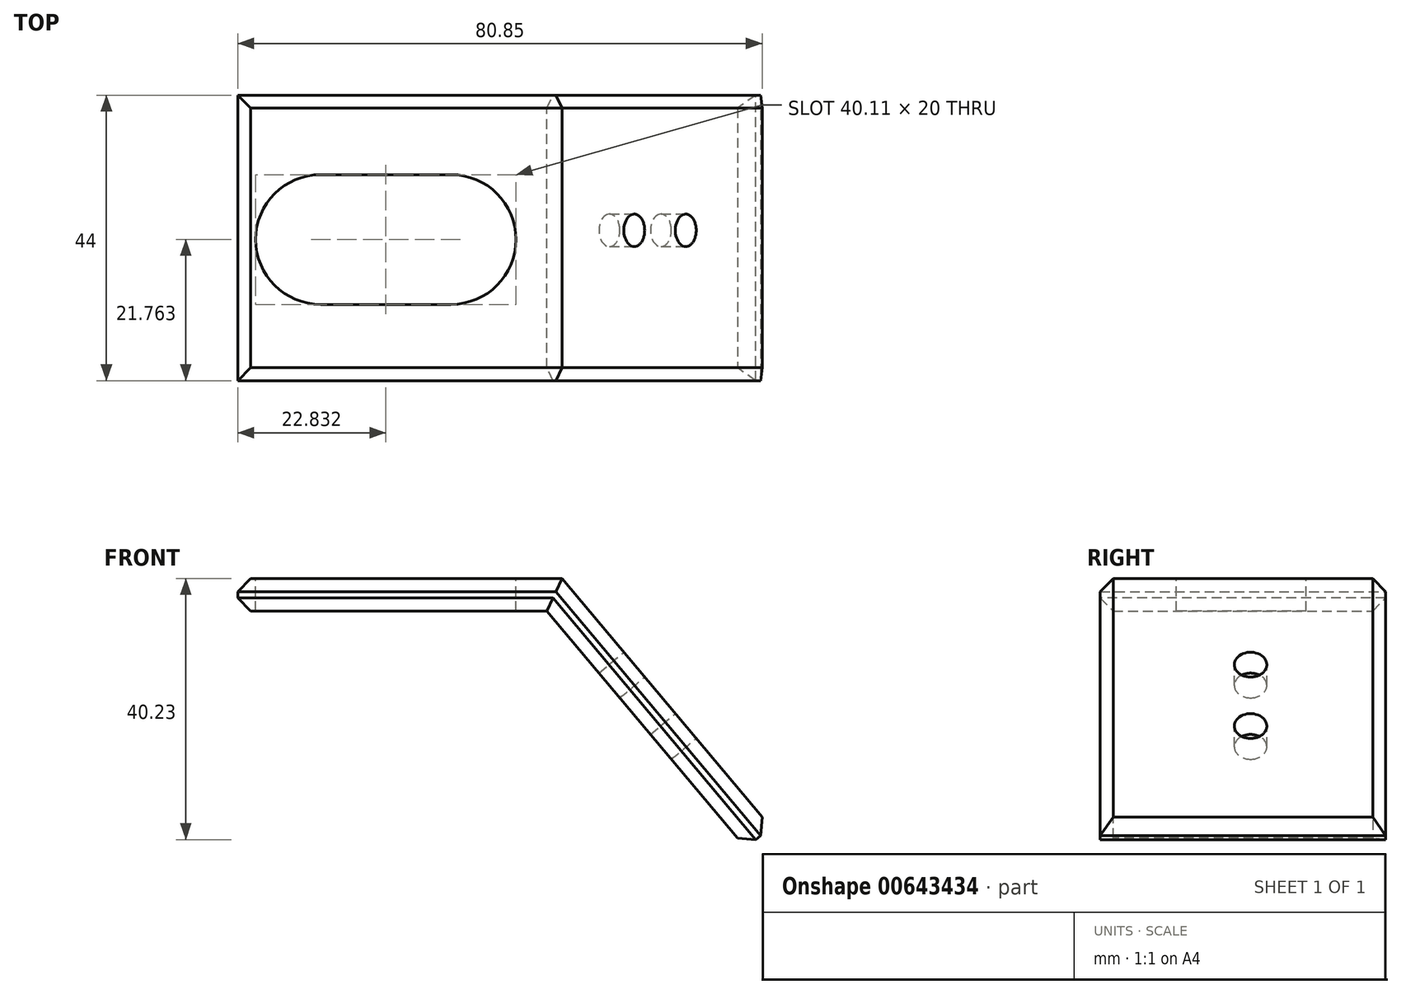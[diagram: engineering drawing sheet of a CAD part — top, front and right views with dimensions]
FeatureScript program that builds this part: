
annotation { "Feature Type Name" : "Feature", "Feature Type Description" : "" }
export const myFeature = defineFeature(function(context is Context, id is Id, definition is map)
    precondition{}
    {
        {
            var Q0;
            Q0=qCreatedBy(makeId("Front.planeOp"),FACE);
            var sketch = newSketch(context, id + "F0", { "sketchPlane" : qUnion([Q0])});
            skLineSegment(sketch, "E0", {"start": v(0, 0) * mm, "end": v(50, 0) * mm});
            skLineSegment(sketch, "E1", {"start": v(50, 0) * mm, "end": v(82.14, -38.3) * mm});
            skLineSegment(sketch, "E2.0", {"start": v(47.67, -5) * mm, "end": v(78.3, -41.52) * mm});
            skLineSegment(sketch, "E2.1", {"start": v(0, -5) * mm, "end": v(47.67, -5) * mm});
            skLineSegment(sketch, "E3", {"start": v(0, 0) * mm, "end": v(0, -5) * mm});
            skLineSegment(sketch, "E4", {"start": v(78.3, -41.52) * mm, "end": v(82.14, -38.3) * mm});
            skSolve(sketch);
        }
        {
            var Q0;
            Q0 = qSketchRegion(id + "F0", true);
            extrude(context, id + "F1", {"entities" : qUnion([Q0]), "depth" : 44 * mm, "offsetDistance" : 25 * mm});
        }
        {
            var Q0;
            Q0=makeQuery(id+"F1.opExtrude","SWEPT_FACE",FACE,{"disambiguationData":[OSD([sQuery(id+"F0.wireOp",EDGE,"E0")])]});
            var sketch = newSketch(context, id + "F2", { "sketchPlane" : qUnion([Q0])});
            skLineSegment(sketch, "E5", {"start": v(12.78, -22.24) * mm, "end": v(32.89, -22.24) * mm});
            skArc(sketch, "E6.0.startCap", {"start": v(12.78, -32.24) * mm, "mid": v(2.78, -22.24) * mm, "end": v(12.78, -12.24) * mm});
            skArc(sketch, "E6.0.endCap", {"start": v(32.89, -12.24) * mm, "mid": v(42.89, -22.24) * mm, "end": v(32.89, -32.24) * mm});
            skLineSegment(sketch, "E6.0.left", {"start": v(12.78, -12.24) * mm, "end": v(32.89, -12.24) * mm});
            skLineSegment(sketch, "E6.0.right", {"start": v(12.78, -32.24) * mm, "end": v(32.89, -32.24) * mm});
            skSolve(sketch);
        }
        {
            var Q0;
            Q0 = qSketchRegion(id + "F2", true);
            extrude(context, id + "F3", {"entities" : qUnion([Q0]), "operationType" : NewBodyOperationType.REMOVE, "oppositeDirection" : true, "depth" : 25 * mm, "offsetDistance" : 25 * mm});
        }
        {
            var Q0;
            Q0=makeQuery(id+"F1.opExtrude","SWEPT_FACE",FACE,{"disambiguationData":[OSD([sQuery(id+"F0.wireOp",EDGE,"E1")])]});
            var sketch = newSketch(context, id + "F4", { "sketchPlane" : qUnion([Q0])});
            skPoint(sketch, "E7", {"position": v(-20.82, -49.46) * mm});
            skPoint(sketch, "E8", {"position": v(-20.82, -61.8) * mm});
            skSolve(sketch);
        }
        {
            var Q0;
            Q0=sQuery(id+"F4.wireOp",VERTEX,"E7");
            var Q1;
            Q1=sQuery(id+"F4.wireOp",VERTEX,"E8");
            var Q2;
            Q2=makeQuery(id+"F1.opExtrude","SWEPT_BODY",BODY,{"disambiguationData":[OSD([sQuery(id+"F0.wireOp",EDGE,"E0"),sQuery(id+"F0.wireOp",EDGE,"E1"),sQuery(id+"F0.wireOp",EDGE,"E2.0"),sQuery(id+"F0.wireOp",EDGE,"E2.1"),sQuery(id+"F0.wireOp",EDGE,"E3"),sQuery(id+"F0.wireOp",EDGE,"E4")])]});
            hole(context, id + "F5", {"style" : HoleStyle.SIMPLE, "endStyle" : HoleEndStyle.THROUGH, "holeDiameter" : 5 * mm, "majorDiameter" : 5 * mm, "isTappedThrough" : true, "tappedDepth" : 12 * mm, "tapClearance" : 3, "locations" : qUnion([Q0, Q1]), "scope" : qUnion([Q2])});
        }
        {
            var Q0;
            Q0=makeQuery(id+"F1.opExtrude","CAP_EDGE",EDGE,{"disambiguationData":[OSD([sQuery(id+"F0.wireOp",EDGE,"E1")])],"isStart":false});
            var Q1;
            Q1=makeQuery(id+"F1.opExtrude","CAP_EDGE",EDGE,{"disambiguationData":[OSD([sQuery(id+"F0.wireOp",EDGE,"E2.0")])],"isStart":false});
            var Q2;
            Q2=makeQuery(id+"F1.opExtrude","SWEPT_EDGE",EDGE,{"disambiguationData":[OSD([sQuery(id+"F0.wireOp",EDGE,"E2.0"),sQuery(id+"F0.wireOp",EDGE,"E4")])]});
            var Q3;
            Q3=makeQuery(id+"F1.opExtrude","SWEPT_EDGE",EDGE,{"disambiguationData":[OSD([sQuery(id+"F0.wireOp",EDGE,"E1"),sQuery(id+"F0.wireOp",EDGE,"E4")])]});
            var Q4;
            Q4=makeQuery(id+"F1.opExtrude","CAP_EDGE",EDGE,{"disambiguationData":[OSD([sQuery(id+"F0.wireOp",EDGE,"E1")])],"isStart":true});
            var Q5;
            Q5=makeQuery(id+"F1.opExtrude","CAP_EDGE",EDGE,{"disambiguationData":[OSD([sQuery(id+"F0.wireOp",EDGE,"E2.0")])],"isStart":true});
            chamfer(context, id + "F6", {"entities" : qUnion([Q0, Q1, Q2, Q3, Q4, Q5]), "width" : 2 * mm, "tangentPropagation" : true});
        }
        {
            var Q0;
            Q0=makeQuery(id+"F1.opExtrude","CAP_EDGE",EDGE,{"disambiguationData":[OSD([sQuery(id+"F0.wireOp",EDGE,"E0")])],"isStart":true});
            var Q1;
            Q1=makeQuery(id+"F1.opExtrude","CAP_EDGE",EDGE,{"disambiguationData":[OSD([sQuery(id+"F0.wireOp",EDGE,"E2.1")])],"isStart":true});
            var Q2;
            Q2=makeQuery(id+"F1.opExtrude","SWEPT_EDGE",EDGE,{"disambiguationData":[OSD([sQuery(id+"F0.wireOp",EDGE,"E0"),sQuery(id+"F0.wireOp",EDGE,"E3")])]});
            var Q3;
            Q3=makeQuery(id+"F1.opExtrude","SWEPT_EDGE",EDGE,{"disambiguationData":[OSD([sQuery(id+"F0.wireOp",EDGE,"E2.1"),sQuery(id+"F0.wireOp",EDGE,"E3")])]});
            var Q4;
            Q4=makeQuery(id+"F1.opExtrude","CAP_EDGE",EDGE,{"disambiguationData":[OSD([sQuery(id+"F0.wireOp",EDGE,"E0")])],"isStart":false});
            var Q5;
            Q5=makeQuery(id+"F1.opExtrude","CAP_EDGE",EDGE,{"disambiguationData":[OSD([sQuery(id+"F0.wireOp",EDGE,"E2.1")])],"isStart":false});
            chamfer(context, id + "F7", {"entities" : qUnion([Q0, Q1, Q2, Q3, Q4, Q5]), "width" : 2 * mm, "tangentPropagation" : true});
        }
    });
